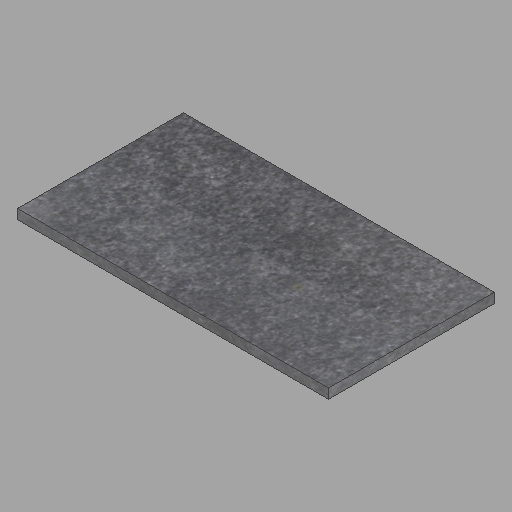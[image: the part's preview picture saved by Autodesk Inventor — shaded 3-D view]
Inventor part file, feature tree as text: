
AUTODESK INVENTOR PART (.ipt)
format: ipt  version: 2023 (Build 270158030, 158C)  size: 218,112 bytes
history: native  units: in
note: dims shown in document units (in); Inventor stores cm internally (conversion verified against a paired STEP export)
features: extrude x1, sketch x1
ambient origin geometry x8: Origin, YZ Plane, XZ Plane, XY Plane, X Axis, Y Axis, Z Axis, Center Point
bodies: Solid1 (feature_tree)
feature tree (2):
  extrude  "Extrusion1"  Depth=34.0in
  sketch  "Sketch1"  dims[d0=63.75in d1=34.0in d2=2.0in d3=0.0in]
